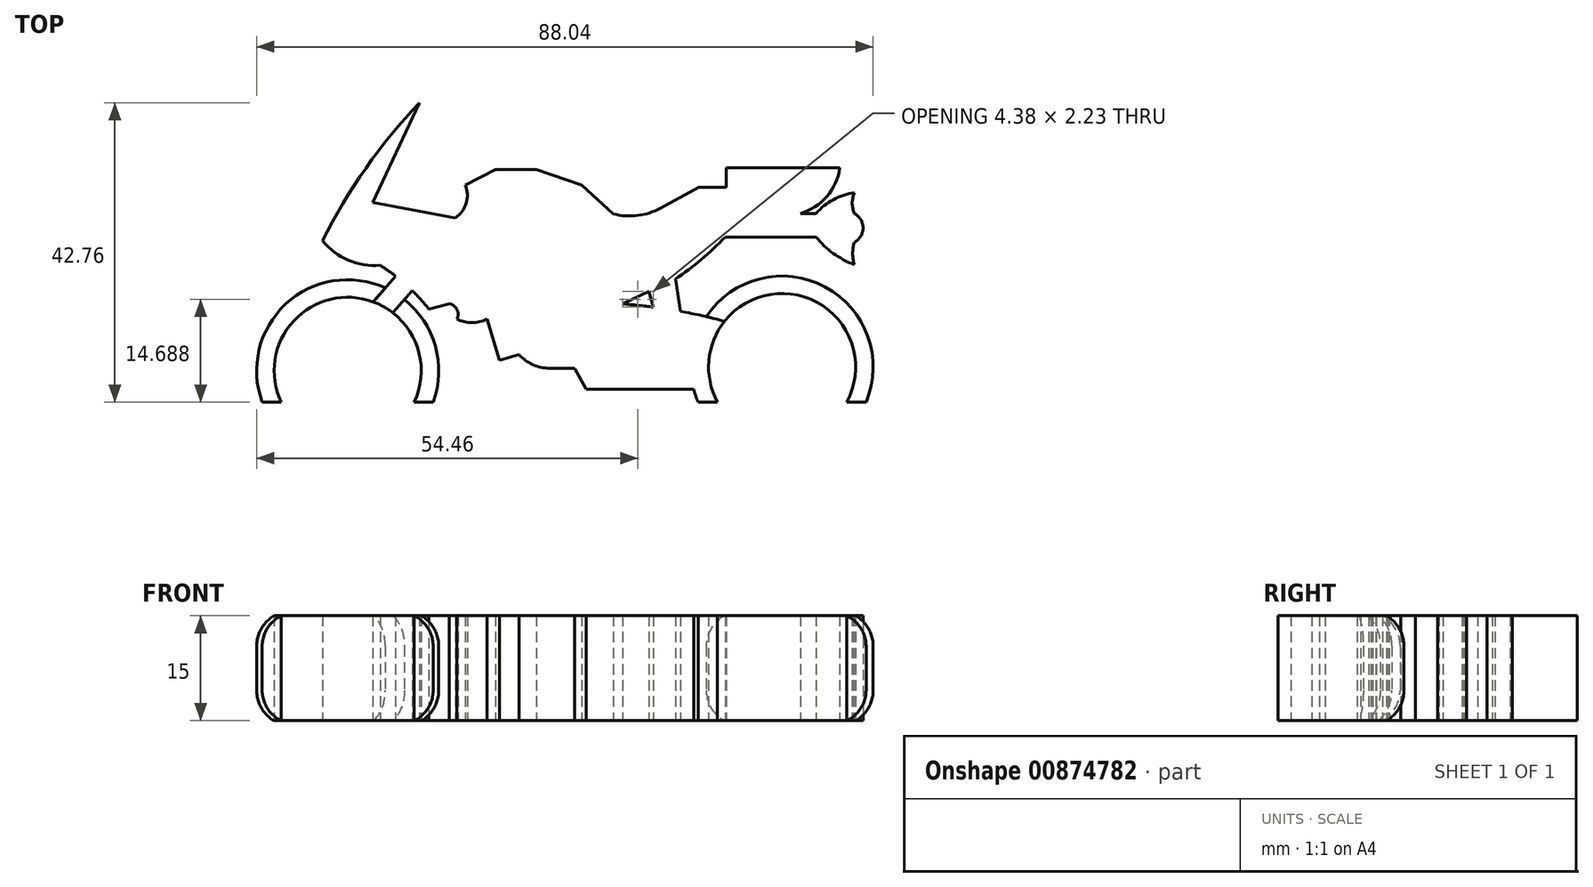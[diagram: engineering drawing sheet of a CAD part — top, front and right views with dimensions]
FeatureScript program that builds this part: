
annotation { "Feature Type Name" : "Feature", "Feature Type Description" : "" }
export const myFeature = defineFeature(function(context is Context, id is Id, definition is map)
    precondition{}
    {
        {
            var Q0;
            Q0=qCreatedBy(makeId("Top.planeOp"),FACE);
            var sketch = newSketch(context, id + "F0", { "sketchPlane" : qUnion([Q0])});
            skArc(sketch, "E0", {"start": v(-23.13, 28.74) * mm, "mid": v(-30.8, 19.4) * mm, "end": v(-36.98, 9.02) * mm});
            skLineSegment(sketch, "E1", {"start": v(-23.13, 28.74) * mm, "end": v(-29.8, 14.5) * mm});
            skLineSegment(sketch, "E2", {"start": v(-29.8, 14.5) * mm, "end": v(-18.04, 12.3) * mm});
            skArc(sketch, "E3", {"start": v(-18.04, 12.3) * mm, "mid": v(-16.49, 14.38) * mm, "end": v(-16.59, 16.98) * mm});
            skLineSegment(sketch, "E4", {"start": v(-16.59, 16.98) * mm, "end": v(-12.32, 19.18) * mm});
            skLineSegment(sketch, "E5", {"start": v(-12.32, 19.18) * mm, "end": v(-6.47, 19.18) * mm});
            skLineSegment(sketch, "E6", {"start": v(-6.47, 19.18) * mm, "end": v(0, 16.98) * mm});
            skLineSegment(sketch, "E7", {"start": v(0, 16.98) * mm, "end": v(4.53, 12.85) * mm});
            skArc(sketch, "E8", {"start": v(4.53, 12.85) * mm, "mid": v(7.99, 12.62) * mm, "end": v(11.28, 13.67) * mm});
            skLineSegment(sketch, "E9", {"start": v(11.28, 13.67) * mm, "end": v(16.7, 16.62) * mm});
            skLineSegment(sketch, "E10", {"start": v(16.7, 16.62) * mm, "end": v(20.64, 16.62) * mm});
            skLineSegment(sketch, "E11", {"start": v(20.64, 16.62) * mm, "end": v(20.64, 19.45) * mm});
            skLineSegment(sketch, "E12", {"start": v(20.64, 19.45) * mm, "end": v(36.88, 19.45) * mm});
            skArc(sketch, "E13", {"start": v(31.23, 12.92) * mm, "mid": v(35.03, 15.34) * mm, "end": v(36.88, 19.45) * mm});
            skLineSegment(sketch, "E14", {"start": v(31.23, 12.92) * mm, "end": v(33.5, 12.92) * mm});
            skArc(sketch, "E15", {"start": v(38.94, 15.87) * mm, "mid": v(35.95, 14.9) * mm, "end": v(33.5, 12.92) * mm});
            skArc(sketch, "E16", {"start": v(38.94, 15.87) * mm, "mid": v(38.65, 14.4) * mm, "end": v(38.94, 12.92) * mm});
            skArc(sketch, "E17", {"start": v(38.94, 8.79) * mm, "mid": v(40.2, 10.85) * mm, "end": v(38.94, 12.92) * mm});
            skArc(sketch, "E18", {"start": v(38.94, 8.79) * mm, "mid": v(38.71, 7.2) * mm, "end": v(38.94, 5.62) * mm});
            skArc(sketch, "E19", {"start": v(33.5, 9.54) * mm, "mid": v(35.95, 7.2) * mm, "end": v(38.94, 5.62) * mm});
            skLineSegment(sketch, "E20", {"start": v(33.5, 9.54) * mm, "end": v(20.5, 9.54) * mm});
            skArc(sketch, "E21", {"start": v(13.41, 3.56) * mm, "mid": v(17.11, 6.37) * mm, "end": v(20.5, 9.54) * mm});
            skArc(sketch, "E22", {"start": v(18, -1.86) * mm, "mid": v(16.05, -1.43) * mm, "end": v(14.1, -1.05) * mm});
            skArc(sketch, "E23", {"start": v(28.21, -12.15) * mm, "mid": v(29.25, -12.12) * mm, "end": v(30.22, -11.75) * mm});
            skLineSegment(sketch, "E24", {"start": v(16.37, -12.15) * mm, "end": v(0.67, -12.15) * mm});
            skLineSegment(sketch, "E25", {"start": v(0.67, -12.15) * mm, "end": v(-1, -9.18) * mm});
            skLineSegment(sketch, "E26", {"start": v(-1, -9.18) * mm, "end": v(-4.52, -9.18) * mm});
            skArc(sketch, "E27", {"start": v(-8.95, -7.24) * mm, "mid": v(-6.94, -8.67) * mm, "end": v(-4.52, -9.18) * mm});
            skLineSegment(sketch, "E28", {"start": v(-8.95, -7.24) * mm, "end": v(-11.72, -8.08) * mm});
            skLineSegment(sketch, "E29", {"start": v(-11.72, -8.08) * mm, "end": v(-13.51, -2.18) * mm});
            skArc(sketch, "E30", {"start": v(-17.8, -2.18) * mm, "mid": v(-15.66, -2.69) * mm, "end": v(-13.51, -2.18) * mm});
            skArc(sketch, "E31", {"start": v(-17.8, -2.18) * mm, "mid": v(-17.8, -0.8) * mm, "end": v(-18.9, 0.03) * mm});
            skLineSegment(sketch, "E32", {"start": v(-18.9, 0.03) * mm, "end": v(-21.81, -0.73) * mm});
            skArc(sketch, "E33", {"start": v(-21.81, -0.73) * mm, "mid": v(-22.96, 0.62) * mm, "end": v(-24.2, 1.9) * mm});
            skArc(sketch, "E34", {"start": v(-36.98, 9.02) * mm, "mid": v(-33.3, 6.24) * mm, "end": v(-28.76, 5.51) * mm});
            skLineSegment(sketch, "E35", {"start": v(13.41, 3.56) * mm, "end": v(14.1, -1.05) * mm});
            skLineSegment(sketch, "E36", {"start": v(9.63, 1.78) * mm, "end": v(10.24, -0.45) * mm});
            skLineSegment(sketch, "E37", {"start": v(-28.03, 2.29) * mm, "end": v(-26.57, 3.97) * mm});
            skLineSegment(sketch, "E38", {"start": v(-26.57, 3.97) * mm, "end": v(-24.2, 1.9) * mm});
            skArc(sketch, "E39.trimOffspring", {"start": v(-26.57, 3.97) * mm, "mid": v(-27.65, 4.77) * mm, "end": v(-28.76, 5.51) * mm});
            skArc(sketch, "E40.trimOffspring", {"start": v(10.24, -0.45) * mm, "mid": v(8.05, -0.2) * mm, "end": v(5.86, 0) * mm});
            skLineSegment(sketch, "E41", {"start": v(9.63, 1.78) * mm, "end": v(5.86, 0) * mm});
            skLineSegment(sketch, "E42", {"start": v(-22.96, 0.62) * mm, "end": v(-23.54, -0.34) * mm});
            skPoint(sketch, "E43.end.orphan", {"position": v(-33.4, -3.91) * mm});
            skLineSegment(sketch, "E44.trimOffspring", {"start": v(39.12, -9.28) * mm, "end": v(39.13, -9.28) * mm});
            skArc(sketch, "E45", {"start": v(-21.2, -14.02) * mm, "mid": v(-33.4, 3.45) * mm, "end": v(-45.62, -14.02) * mm});
            skArc(sketch, "E46", {"start": v(-23.9, -14.02) * mm, "mid": v(-33.4, 0.95) * mm, "end": v(-42.91, -14.02) * mm});
            skLineSegment(sketch, "E47", {"start": v(-21.2, -14.02) * mm, "end": v(-23.9, -14.02) * mm});
            skLineSegment(sketch, "E48.trimOffspring", {"start": v(-42.91, -14.02) * mm, "end": v(-45.62, -14.02) * mm});
            skLineSegment(sketch, "E49", {"start": v(-24.2, 1.9) * mm, "end": v(-25.31, 0.62) * mm});
            skPoint(sketch, "E50.orphan", {"position": v(-26.57, -0.83) * mm});
            skArc(sketch, "E51", {"start": v(16.02, -12.15) * mm, "mid": v(16.3, -13.1) * mm, "end": v(16.63, -14.02) * mm});
            skArc(sketch, "E52", {"start": v(37.86, -14.02) * mm, "mid": v(28.63, 1.49) * mm, "end": v(19.4, -14.02) * mm});
            skLineSegment(sketch, "E53", {"start": v(16.63, -14.02) * mm, "end": v(19.4, -14.02) * mm});
            skArc(sketch, "E54.trimOffspring", {"start": v(40.63, -14.02) * mm, "mid": v(34.76, 2.45) * mm, "end": v(17.8, -1.82) * mm});
            skLineSegment(sketch, "E55.trimOffspring", {"start": v(37.86, -14.02) * mm, "end": v(40.63, -14.02) * mm});
            skSolve(sketch);
        }
        {
            var Q0;
            Q0 = qSketchRegion(id + "F0", true);
            extrude(context, id + "F1", {"entities" : qUnion([Q0]), "depth" : 15 * mm, "offsetDistance" : 25 * mm});
        }
        {
            var Q0;
            {var subQ0=sQuery(id+"F0.wireOp",EDGE,"E45");Q0=makeQuery(id+"F1.opExtrude","CAP_EDGE",EDGE,{"disambiguationData":[OSD([subQ0]),TDD([makeQuery(id+"F0.imprint","IMPRINT",EDGE,{"disambiguationData":[TD([[makeQuery(id+"F0.imprint","INTERSECT",VERTEX,{"derivedFrom":[sQuery(id+"F0.wireOp",EDGE,"E37"),subQ0]}),-1.0]])],"derivedFrom":subQ0})])],"isStart":false});}
            var Q1;
            {var subQ0=sQuery(id+"F0.wireOp",EDGE,"E45");Q1=makeQuery(id+"F1.opExtrude","CAP_EDGE",EDGE,{"disambiguationData":[OSD([subQ0]),TDD([makeQuery(id+"F0.imprint","IMPRINT",EDGE,{"disambiguationData":[TD([[makeQuery(id+"F0.imprint","INTERSECT",VERTEX,{"derivedFrom":[sQuery(id+"F0.wireOp",EDGE,"E37"),subQ0]}),-1.0]])],"derivedFrom":subQ0})])],"isStart":true});}
            var Q2;
            Q2=makeQuery(id+"F1.opExtrude","CAP_EDGE",EDGE,{"disambiguationData":[OSD([sQuery(id+"F0.wireOp",EDGE,"E54.trimOffspring")])],"isStart":true});
            var Q3;
            Q3=makeQuery(id+"F1.opExtrude","CAP_EDGE",EDGE,{"disambiguationData":[OSD([sQuery(id+"F0.wireOp",EDGE,"E54.trimOffspring")])],"isStart":false});
            var Q4;
            {var subQ0=sQuery(id+"F0.wireOp",EDGE,"E45");Q4=makeQuery(id+"F1.opExtrude","CAP_EDGE",EDGE,{"disambiguationData":[OSD([subQ0]),TDD([makeQuery(id+"F0.imprint","IMPRINT",EDGE,{"disambiguationData":[TD([[makeQuery(id+"F0.imprint","INTERSECT",VERTEX,{"derivedFrom":[subQ0,sQuery(id+"F0.wireOp",EDGE,"E47")]}),-1.0]])],"derivedFrom":subQ0})])],"isStart":false});}
            var Q5;
            {var subQ0=sQuery(id+"F0.wireOp",EDGE,"E45");Q5=makeQuery(id+"F1.opExtrude","CAP_EDGE",EDGE,{"disambiguationData":[OSD([subQ0]),TDD([makeQuery(id+"F0.imprint","IMPRINT",EDGE,{"disambiguationData":[TD([[makeQuery(id+"F0.imprint","INTERSECT",VERTEX,{"derivedFrom":[subQ0,sQuery(id+"F0.wireOp",EDGE,"E47")]}),-1.0]])],"derivedFrom":subQ0})])],"isStart":true});}
            fillet(context, id + "F2", {"entities" : qUnion([Q0, Q1, Q2, Q3, Q4, Q5]), "radius" : 5 * mm, "tangentPropagation" : true, "allowEdgeOverflow" : false});
        }
    });
